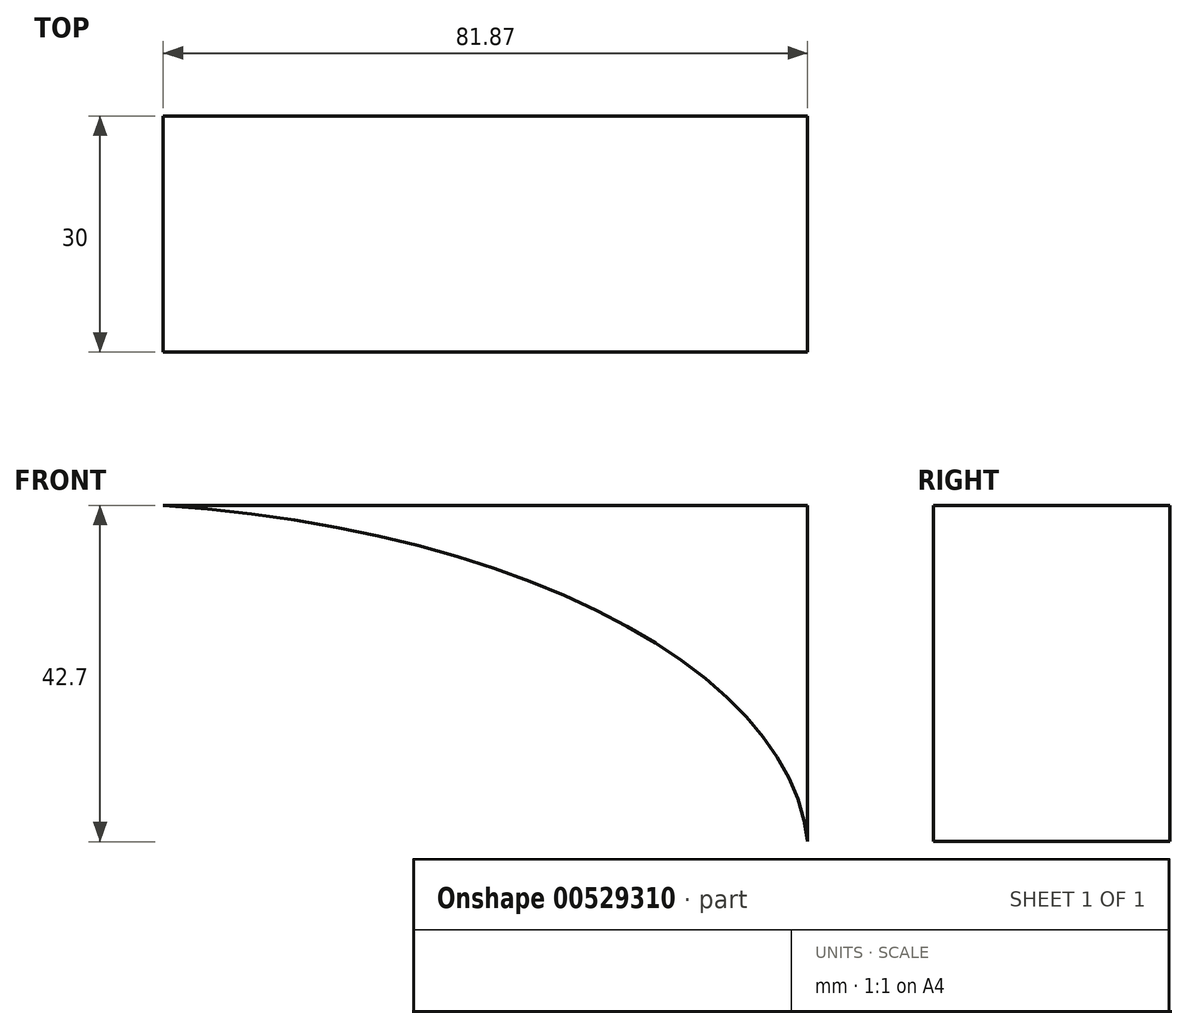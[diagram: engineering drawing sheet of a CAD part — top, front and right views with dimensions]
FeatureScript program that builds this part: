
annotation { "Feature Type Name" : "Feature", "Feature Type Description" : "" }
export const myFeature = defineFeature(function(context is Context, id is Id, definition is map)
    precondition{}
    {
        {
            var Q0;
            Q0=qCreatedBy(makeId("Front.planeOp"),FACE);
            var sketch = newSketch(context, id + "F0", { "sketchPlane" : qUnion([Q0])});
            skLineSegment(sketch, "E0", {"start": v(-95, 45) * mm, "end": v(95, 45) * mm});
            skLineSegment(sketch, "E1", {"start": v(95, 45) * mm, "end": v(95, -20) * mm});
            skLineSegment(sketch, "E2", {"start": v(95, -20) * mm, "end": v(-95, -20) * mm});
            skLineSegment(sketch, "E3", {"start": v(-95, -20) * mm, "end": v(-95, 45) * mm});
            skEllipse(sketch, "E4", {"center": v(0, 0) * mm, "majorRadius": 95.12 * mm, "minorRadius": 45.44 * mm, "majorAxis": v(-1, 0)});
            skSolve(sketch);
        }
        {
            var Q0;
            {var subQ0=sQuery(id+"F0.wireOp",EDGE,"E4");var subQ7=sQuery(id+"F0.wireOp",EDGE,"E0");var subQ8=makeQuery(id+"F0.imprint","INTERSECT",VERTEX,{"disambiguationData":[OD(0.0)],"derivedFrom":[subQ7,subQ0]});Q0=makeQuery(id+"F0.imprint","IMPRINT",FACE,{"disambiguationData":[TD([[makeQuery(id+"F0.imprint","IMPRINT",EDGE,{"disambiguationData":[TD([[subQ8,-1.0]])],"derivedFrom":subQ7}),-1.0]])]});}
            extrude(context, id + "F1", {"entities" : qUnion([Q0]), "endBound" : BoundingType.SYMMETRIC, "depth" : 30 * mm, "offsetDistance" : 25 * mm});
        }
    });
